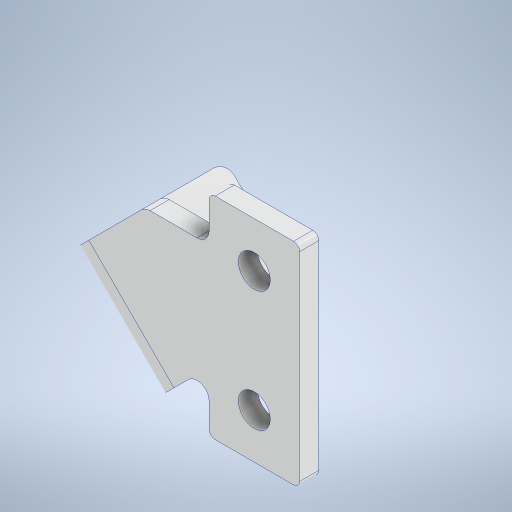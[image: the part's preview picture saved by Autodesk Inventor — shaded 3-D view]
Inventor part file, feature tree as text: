
AUTODESK INVENTOR PART (.ipt)
format: ipt  version: 2024 (Build 280153000, 153)  size: 330,240 bytes
history: native  units: mm
features: sheet_metal_op x4, sketch x3, fillet x3, hole x2, other x2
ambient origin geometry x8: Origin, YZ Plane, XZ Plane, XY Plane, X Axis, Y Axis, Z Axis, Center Point
bodies: Body1 (feature_tree)
feature tree (14):
  sketch  "Sketch1"  dims[d1=28.0mm d2=21.5mm d3=35.0mm d5=20.0mm]
  sheet_metal_op  "Face2"
  sheet_metal_op  "Flange1"
  fillet  "Fillet1"  Radius=30.0mm
  hole  "Hole2"  [1 undecoded]
  fillet  "Fillet2"  Radius=35.0mm
  fillet  "Fillet3"  Radius=20.0mm
  hole  "Hole1"  [1 undecoded]
  other  "Plate2"
  sketch  "Sketch2"  dims[d6=7.5mm d7=7.5mm]
  other  "Plate3"
  sheet_metal_op  "Bend1"
  sheet_metal_op  "Corner1"
  sketch  "Sketch3"  dims[d8=7.5mm d11=20.0mm d12=20.0mm d13=3.175mm d14=3.175mm d15=1.5875mm d16=6.35mm d17=3.175mm d18=25.0mm d19=90.0deg d20=3.175mm d21=12.7mm d22=3.175mm d23=3.175mm d24=2.0mm d25=2.0mm d26=1.0mm d27=5.3mm d28=6.0mm d29=4.0mm d30=2.0mm d31=90.0deg d32=3.175mm d33=20.594885mm d34=6.3mm d35=6.0mm d36=4.0mm d37=2.0mm d38=90.0deg d39=8.0mm d40=20.594885mm]
note: 2 required parameter values undecoded (feature->parameter linkage not recoverable at this tier; creation-order binding heuristic only, values carry confidence <= 0.55)
